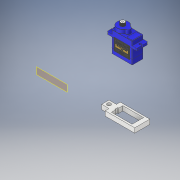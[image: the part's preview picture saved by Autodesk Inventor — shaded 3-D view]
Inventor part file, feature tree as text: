
AUTODESK INVENTOR PART (.ipt)
format: ipt  version: 2019 (Build 230136000, 136)  size: 1,603,072 bytes
history: native  units: in
note: dims shown in document units (in); Inventor stores cm internally (conversion verified against a paired STEP export)
features: other x13, sketch x4, extrude x3, plane x2
ambient origin geometry x8: Origin, YZ Plane, XZ Plane, XY Plane, X Axis, Y Axis, Z Axis, Center Point
bodies: Solid1 (feature_tree), Solid2 (feature_tree), Solid3 (feature_tree), Solid4 (feature_tree), Solid5 (feature_tree), Solid6 (feature_tree), Solid7 (feature_tree), Solid8 (feature_tree), Solid9 (feature_tree), Solid10 (feature_tree), Solid11 (feature_tree), Solid12 (feature_tree), Solid13 (feature_tree), Solid14 (feature_tree)
feature tree (22):
  plane  "Work Plane1"
  sketch  "Sketch1"  dims[d0=3.0in d17=0.1969in d18=0.0in]
  plane  "Work Plane3"
  extrude  "Extrusion4"  Depth=0.1969in TaperAngle=0.0deg
  extrude  "Extrusion5"  Depth=0.0394in
  extrude  "Extrusion6"  Depth=0.1181in TaperAngle=0.0deg
  sketch  "Sketch6"  dims[d19=0.4882in d20=0.0394in]
  sketch  "Sketch7"  dims[d21=0.1181in d22=0.1969in d23=0.0in]
  sketch  "Sketch8"  dims[d24=0.315in d25=0.315in d26=0.1575in d27=0.1969in d28=0.0in]
  other  "SG90 - Micro Servo 9g - Tower Pro.1-1-solid1"
  other  "SG90 - Micro Servo 9g - Tower Pro.1-1-solid2"
  other  "SG90 - Micro Servo 9g - Tower Pro.1-1-solid3"
  other  "SG90 - Micro Servo 9g - Tower Pro.1-1-solid4"
  other  "SG90 - Micro Servo 9g - Tower Pro.1-1-solid5"
  other  "SG90 - Micro Servo 9g - Tower Pro.1-1-solid6"
  other  "SG90 - Micro Servo 9g - Tower Pro.1-1-solid7"
  other  "SG90 - Micro Servo 9g - Tower Pro.1-1-solid8"
  other  "SG90 - Micro Servo 9g - Tower Pro.1-1-solid9"
  other  "SG90 - Micro Servo 9g - Tower Pro.1-1-solid10"
  other  "SG90 - Micro Servo 9g - Tower Pro.1-1-solid11"
  other  "SG90 - Micro Servo 9g - Tower Pro.1-1-solid12"
  other  "SG90 - Micro Servo 9g - Tower Pro.1-1-solid13"
